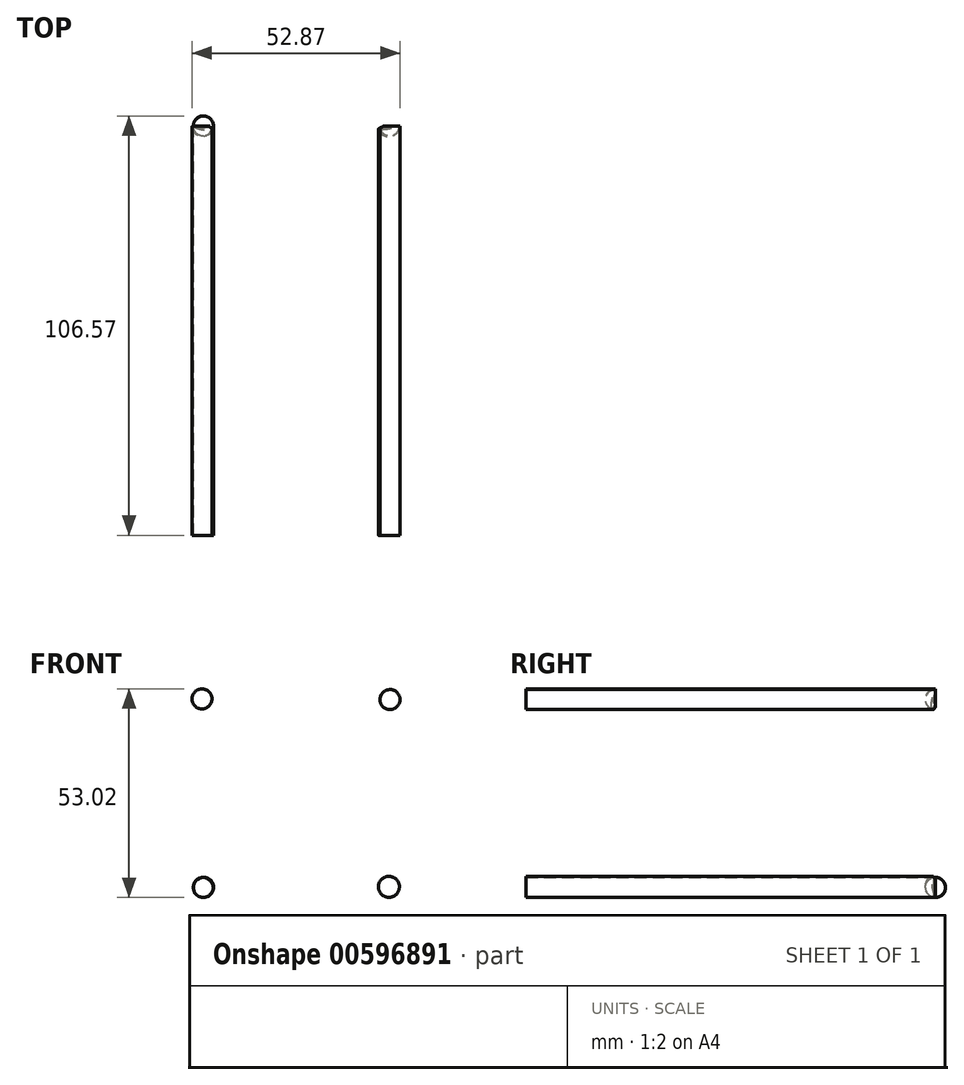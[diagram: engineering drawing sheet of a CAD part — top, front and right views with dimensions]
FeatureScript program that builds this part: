
annotation { "Feature Type Name" : "Feature", "Feature Type Description" : "" }
export const myFeature = defineFeature(function(context is Context, id is Id, definition is map)
    precondition{}
    {
        {
            var Q0;
            Q0=qCreatedBy(makeId("Top.planeOp"),FACE);
            var sketch = newSketch(context, id + "F0", { "sketchPlane" : qUnion([Q0])});
            skArc(sketch, "E0", {"start": v(-33.7, 0) * mm, "mid": v(0, -33.7) * mm, "end": v(33.7, 0) * mm});
            skSolve(sketch);
        }
        {
            var Q0;
            Q0=qCreatedBy(makeId("Top.planeOp"),FACE);
            var sketch = newSketch(context, id + "F1", { "sketchPlane" : qUnion([Q0])});
            skLineSegment(sketch, "E1", {"start": v(-34.1, 0) * mm, "end": v(35.66, 0) * mm});
            skSolve(sketch);
        }
        {
            var Q0;
            Q0=sQuery(id+"F0.wireOp",EDGE,"E0");
            var Q1;
            Q1=sQuery(id+"F1.wireOp",EDGE,"E1");
            revolve(context, id + "F2", {"bodyType" : ToolBodyType.SURFACE, "surfaceEntities" : qUnion([Q0]), "axis" : qUnion([Q1]), "revolveType" : RevolveType.FULL});
        }
        {
            var Q0;
            Q0=qCreatedBy(makeId("Front.planeOp"),FACE);
            var sketch = newSketch(context, id + "F3", { "sketchPlane" : qUnion([Q0])});
            skCircle(sketch, "E2", {"center": v(23.96, 23.66) * mm, "radius": 2.54 * mm});
            skLineSegment(sketch, "E3", {"start": v(23.96, 23.66) * mm, "end": v(22.15, 25.44) * mm});
            skCircle(sketch, "E4", {"center": v(-23.83, 23.82) * mm, "radius": 2.54 * mm});
            skLineSegment(sketch, "E5", {"start": v(-23.83, 23.82) * mm, "end": v(-26.37, 23.7) * mm});
            skCircle(sketch, "E6", {"center": v(23.67, -23.92) * mm, "radius": 2.67 * mm});
            skLineSegment(sketch, "E7", {"start": v(23.67, -23.92) * mm, "end": v(26.2, -23.11) * mm});
            skCircle(sketch, "E8", {"center": v(-23.48, -24.08) * mm, "radius": 2.54 * mm});
            skLineSegment(sketch, "E9", {"start": v(-23.48, -24.08) * mm, "end": v(-26.02, -24.08) * mm});
            skSolve(sketch);
        }
        {
            var Q0;
            Q0 = qSketchRegion(id + "F3", true);
            extrude(context, id + "F4", {"entities" : qUnion([Q0]), "depth" : 104 * mm, "offsetDistance" : 25.4 * mm});
        }
        {
            var Q0;
            Q0=qCreatedBy(makeId("Front.planeOp"),FACE);
            var sketch = newSketch(context, id + "F5", { "sketchPlane" : qUnion([Q0])});
            skArc(sketch, "E10", {"start": v(25.7, 21.81) * mm, "mid": v(25.71, 25.4) * mm, "end": v(22.12, 25.42) * mm});
            skLineSegment(sketch, "E11", {"start": v(25.7, 21.81) * mm, "end": v(22.12, 25.42) * mm});
            skSolve(sketch);
        }
        {
            var Q0;
            Q0 = qSketchRegion(id + "F5", true);
            var Q1;
            Q1=sQuery(id+"F5.wireOp",EDGE,"E11");
            revolve(context, id + "F6", {"operationType" : NewBodyOperationType.ADD, "entities" : qUnion([Q0]), "axis" : qUnion([Q1]), "revolveType" : RevolveType.FULL});
        }
        {
            var Q0;
            Q0=qCreatedBy(makeId("Front.planeOp"),FACE);
            var sketch = newSketch(context, id + "F7", { "sketchPlane" : qUnion([Q0])});
            skArc(sketch, "E12", {"start": v(21.72, -25.77) * mm, "mid": v(25.51, -25.74) * mm, "end": v(25.44, -21.95) * mm});
            skLineSegment(sketch, "E13", {"start": v(25.44, -21.95) * mm, "end": v(21.72, -25.77) * mm});
            skSolve(sketch);
        }
        {
            var Q0;
            Q0=makeQuery(id+"F7.imprint","IMPRINT",FACE,{"disambiguationData":[TD([[makeQuery(id+"F7.imprint","IMPRINT",EDGE,{"derivedFrom":sQuery(id+"F7.wireOp",EDGE,"E12")}),1.0]])]});
            var Q1;
            Q1=sQuery(id+"F7.wireOp",EDGE,"E13");
            revolve(context, id + "F8", {"operationType" : NewBodyOperationType.ADD, "entities" : qUnion([Q0]), "axis" : qUnion([Q1]), "revolveType" : RevolveType.FULL});
        }
        {
            var Q0;
            Q0=qCreatedBy(makeId("Front.planeOp"),FACE);
            var sketch = newSketch(context, id + "F9", { "sketchPlane" : qUnion([Q0])});
            skArc(sketch, "E14", {"start": v(-21.99, 25.54) * mm, "mid": v(-25.63, 25.53) * mm, "end": v(-25.5, 21.89) * mm});
            skLineSegment(sketch, "E15", {"start": v(-21.99, 25.54) * mm, "end": v(-25.5, 21.89) * mm});
            skSolve(sketch);
        }
        {
            var Q0;
            Q0 = qSketchRegion(id + "F9", true);
            var Q1;
            Q1=sQuery(id+"F9.wireOp",EDGE,"E15");
            revolve(context, id + "F10", {"operationType" : NewBodyOperationType.ADD, "entities" : qUnion([Q0]), "axis" : qUnion([Q1]), "revolveType" : RevolveType.FULL});
        }
        {
            var Q0;
            Q0=qCreatedBy(makeId("Front.planeOp"),FACE);
            var sketch = newSketch(context, id + "F11", { "sketchPlane" : qUnion([Q0])});
            skArc(sketch, "E16", {"start": v(-25.3, -22.29) * mm, "mid": v(-25.27, -25.91) * mm, "end": v(-21.64, -25.87) * mm});
            skLineSegment(sketch, "E17", {"start": v(-21.64, -25.87) * mm, "end": v(-25.3, -22.29) * mm});
            skSolve(sketch);
        }
        {
            var Q0;
            Q0=makeQuery(id+"F11.imprint","IMPRINT",FACE,{"disambiguationData":[TD([[makeQuery(id+"F11.imprint","IMPRINT",EDGE,{"derivedFrom":sQuery(id+"F11.wireOp",EDGE,"E16")}),1.0]])]});
            var Q1;
            Q1=sQuery(id+"F11.wireOp",EDGE,"E17");
            revolve(context, id + "F12", {"operationType" : NewBodyOperationType.ADD, "entities" : qUnion([Q0]), "axis" : qUnion([Q1]), "revolveType" : RevolveType.FULL});
        }
    });
